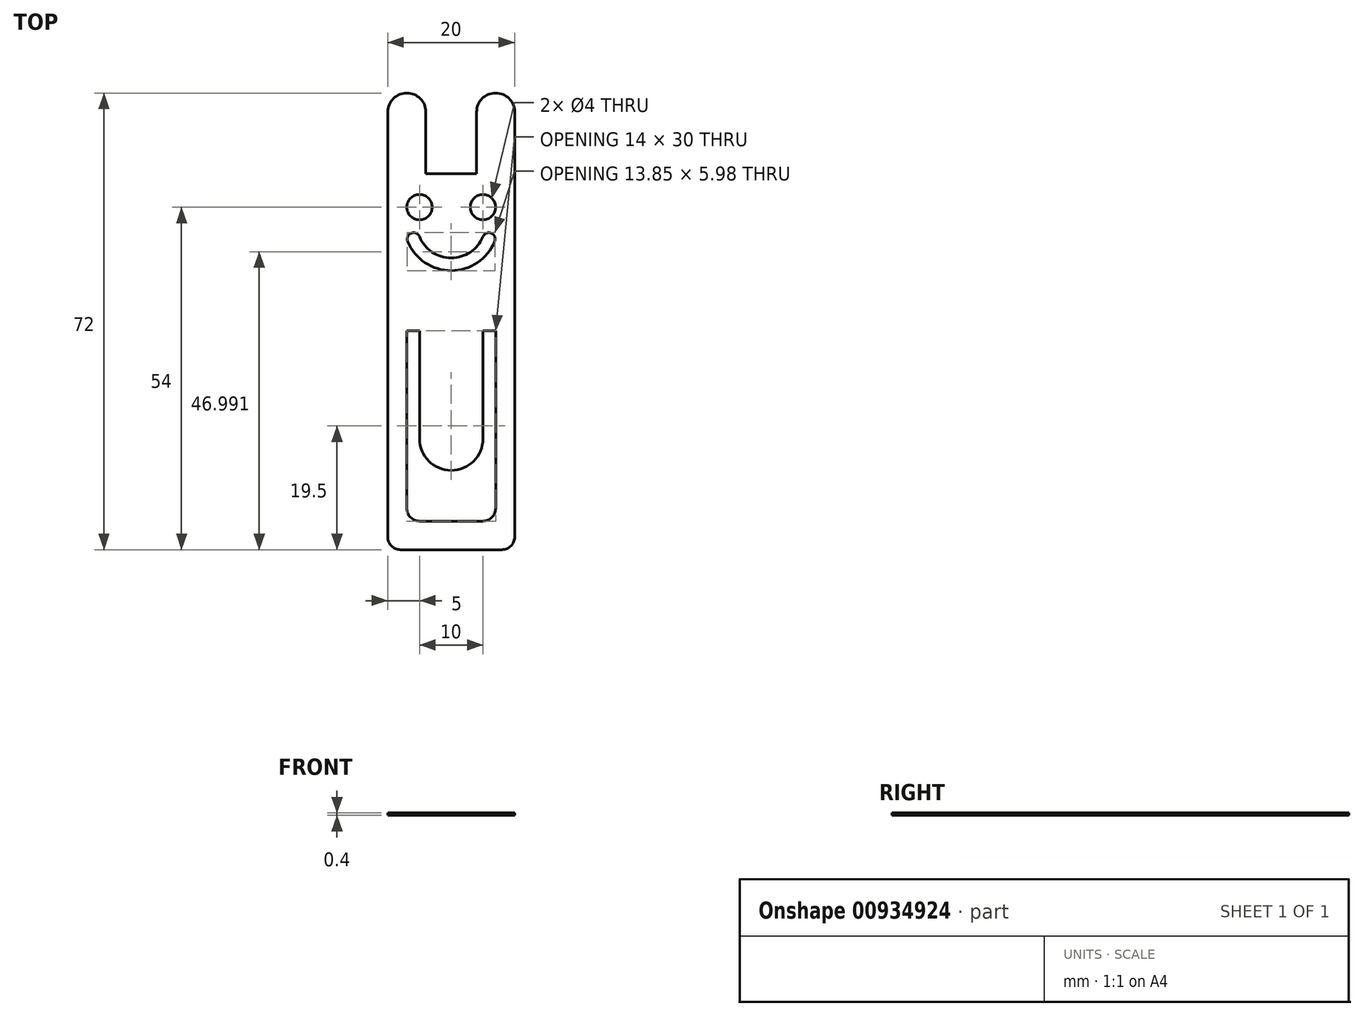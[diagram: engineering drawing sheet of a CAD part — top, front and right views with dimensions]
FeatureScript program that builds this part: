
annotation { "Feature Type Name" : "Feature", "Feature Type Description" : "" }
export const myFeature = defineFeature(function(context is Context, id is Id, definition is map)
    precondition{}
    {
        {
            var Q0;
            Q0=qCreatedBy(makeId("Top.planeOp"),FACE);
            var sketch = newSketch(context, id + "F0", { "sketchPlane" : qUnion([Q0])});
            skLineSegment(sketch, "E0.bottom", {"start": v(10, 34.5) * mm, "end": v(7, 34.5) * mm});
            skLineSegment(sketch, "E0.top", {"start": v(8, -34.5) * mm, "end": v(-8, -34.5) * mm});
            skLineSegment(sketch, "E0.left", {"start": v(10, 34.5) * mm, "end": v(10, -32.5) * mm});
            skLineSegment(sketch, "E0.right", {"start": v(-10, 34.5) * mm, "end": v(-10, -32.5) * mm});
            skPoint(sketch, "E0.middle", {"position": v(0, 0) * mm});
            skLineSegment(sketch, "E1.top", {"start": v(-4, 24.8) * mm, "end": v(4, 24.8) * mm});
            skLineSegment(sketch, "E1.left", {"start": v(-4, 34.5) * mm, "end": v(-4, 24.8) * mm});
            skLineSegment(sketch, "E1.right", {"start": v(4, 34.5) * mm, "end": v(4, 24.8) * mm});
            skLineSegment(sketch, "E2.bottom", {"start": v(-7, 0) * mm, "end": v(7, 0) * mm});
            skLineSegment(sketch, "E2.top", {"start": v(-5, -30) * mm, "end": v(5, -30) * mm});
            skLineSegment(sketch, "E2.left", {"start": v(-7, 0) * mm, "end": v(-7, -28) * mm});
            skLineSegment(sketch, "E2.right", {"start": v(7, 0) * mm, "end": v(7, -28) * mm});
            skLineSegment(sketch, "E3.left", {"start": v(-5, 0) * mm, "end": v(-5, -17) * mm});
            skLineSegment(sketch, "E3.right", {"start": v(5, 0) * mm, "end": v(5, -17) * mm});
            skArc(sketch, "E4", {"start": v(-5, -17) * mm, "mid": v(0, -22) * mm, "end": v(5, -17) * mm});
            skPoint(sketch, "E5.visualSharp", {"position": v(-7, -30) * mm});
            skArc(sketch, "E5.filletArc", {"start": v(-7, -28) * mm, "mid": v(-6.41, -29.41) * mm, "end": v(-5, -30) * mm});
            skPoint(sketch, "E6.visualSharp", {"position": v(7, -30) * mm});
            skArc(sketch, "E6.filletArc", {"start": v(5, -30) * mm, "mid": v(6.41, -29.41) * mm, "end": v(7, -28) * mm});
            skPoint(sketch, "E7.visualSharp", {"position": v(-10, -34.5) * mm});
            skArc(sketch, "E7.filletArc", {"start": v(-10, -32.5) * mm, "mid": v(-9.41, -33.91) * mm, "end": v(-8, -34.5) * mm});
            skPoint(sketch, "E8.visualSharp", {"position": v(10, -34.5) * mm});
            skArc(sketch, "E8.filletArc", {"start": v(8, -34.5) * mm, "mid": v(9.41, -33.91) * mm, "end": v(10, -32.5) * mm});
            skArc(sketch, "E9", {"start": v(-4, 34.5) * mm, "mid": v(-7, 37.5) * mm, "end": v(-10, 34.5) * mm});
            skArc(sketch, "E10", {"start": v(10, 34.5) * mm, "mid": v(7, 37.5) * mm, "end": v(4, 34.5) * mm});
            skCircle(sketch, "E11", {"center": v(-5, 19.5) * mm, "radius": 2 * mm});
            skCircle(sketch, "E12.MirrorC", {"center": v(5, 19.5) * mm, "radius": 2 * mm});
            skArc(sketch, "E13", {"start": v(5, 14.86) * mm, "mid": v(0, 11.5) * mm, "end": v(-5, 14.86) * mm});
            skArc(sketch, "E14.0", {"start": v(6.85, 14.1) * mm, "mid": v(0, 9.5) * mm, "end": v(-6.85, 14.1) * mm});
            skArc(sketch, "E15", {"start": v(-5, 14.86) * mm, "mid": v(-6.3, 15.4) * mm, "end": v(-6.85, 14.1) * mm});
            skArc(sketch, "E16", {"start": v(6.85, 14.1) * mm, "mid": v(6.3, 15.4) * mm, "end": v(5, 14.86) * mm});
            skSolve(sketch);
        }
        {
            var Q0;
            {var subQ0=sQuery(id+"F0.wireOp",EDGE,"E3.left");Q0=makeQuery(id+"F0.imprint","IMPRINT",FACE,{"disambiguationData":[TD([[makeQuery(id+"F0.imprint","IMPRINT",EDGE,{"derivedFrom":subQ0}),1.0]])]});}
            var Q1;
            Q1=makeQuery(id+"F0.imprint","IMPRINT",FACE,{"disambiguationData":[TD([[makeQuery(id+"F0.imprint","IMPRINT",EDGE,{"derivedFrom":sQuery(id+"F0.wireOp",EDGE,"E0.top")}),-1.0]])]});
            extrude(context, id + "F1", {"entities" : qUnion([Q0, Q1]), "flatOperationType" : FlatOperationType.REMOVE, "depth" : 0.4 * mm, "offsetDistance" : 25 * mm, "domain" : OperationDomain.MODEL});
        }
    });
